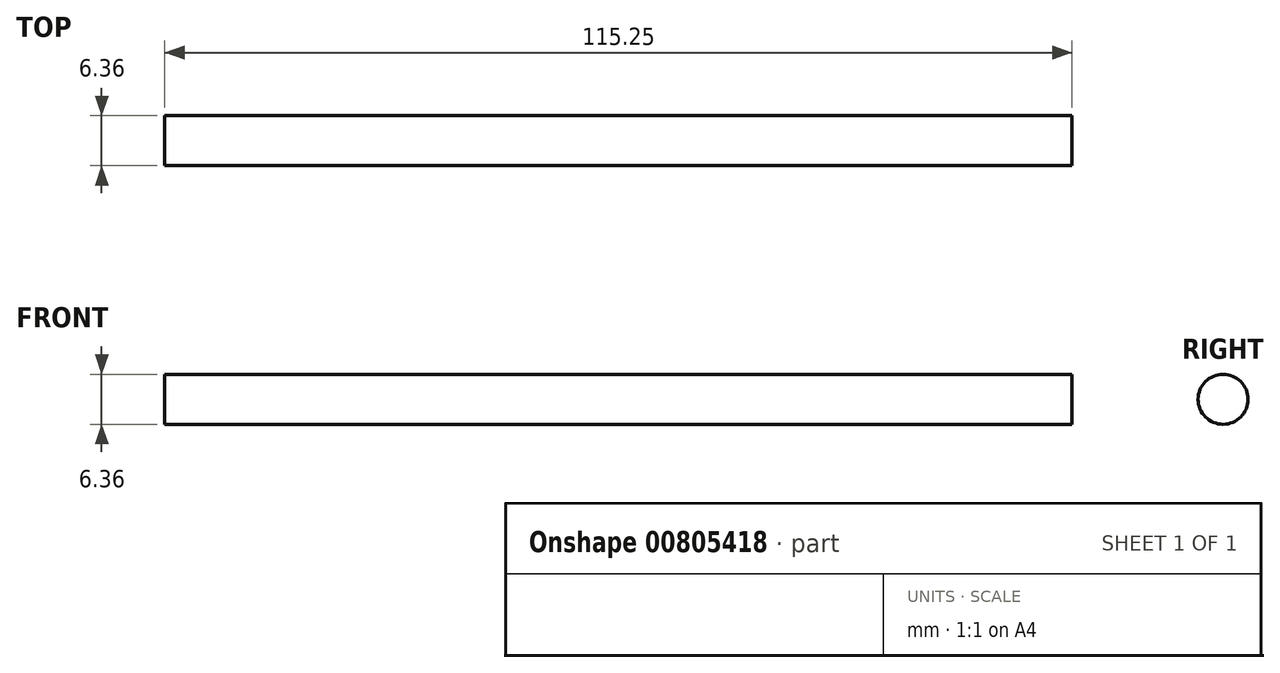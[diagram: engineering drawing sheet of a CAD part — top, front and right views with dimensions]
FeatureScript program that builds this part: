
annotation { "Feature Type Name" : "Feature", "Feature Type Description" : "" }
export const myFeature = defineFeature(function(context is Context, id is Id, definition is map)
    precondition{}
    {
        {
            var Q0;
            Q0=qCreatedBy(makeId("Right.planeOp"),FACE);
            var sketch = newSketch(context, id + "F0", { "sketchPlane" : qUnion([Q0])});
            skCircle(sketch, "E0", {"center": v(0, 0) * mm, "radius": 3.17 * mm});
            skSolve(sketch);
        }
        {
            var Q0;
            Q0 = qSketchRegion(id + "F0", true);
            extrude(context, id + "F1", {"entities" : qUnion([Q0]), "depth" : 115.25 * mm, "offsetDistance" : 25 * mm});
        }
    });
